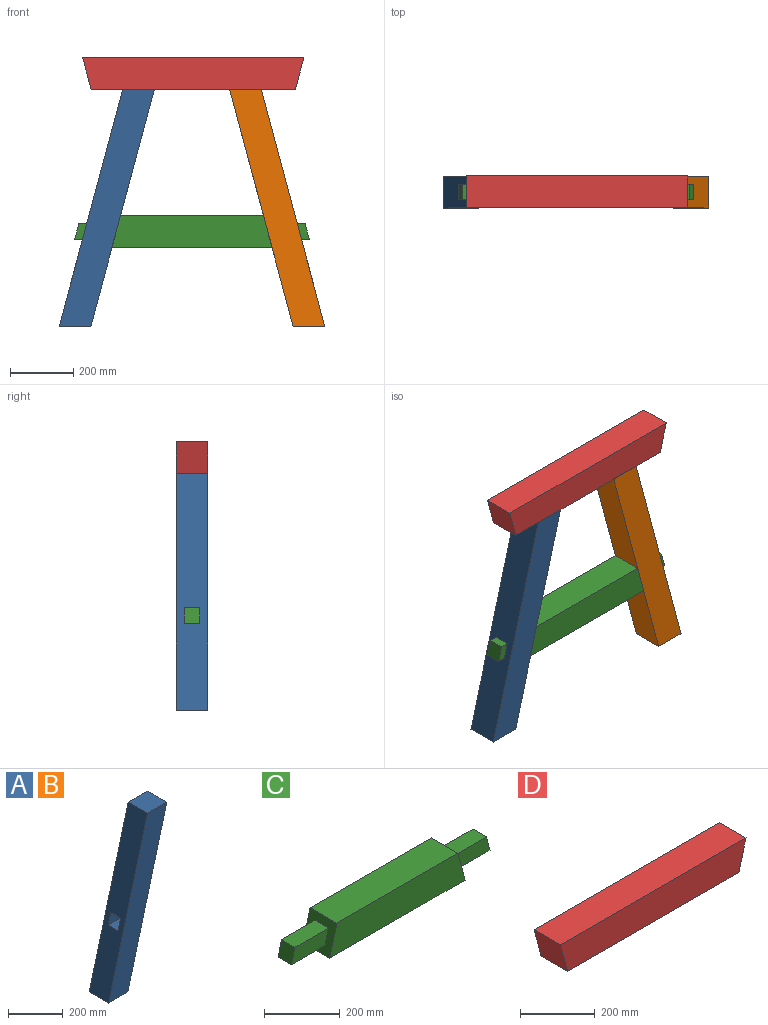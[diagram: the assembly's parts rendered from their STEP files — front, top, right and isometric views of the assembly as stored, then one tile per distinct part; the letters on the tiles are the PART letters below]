
ASSEMBLY  parts=4 mates=3
PART A: 10 faces, bbox 301x100x750 mm
  f0: plane 750x200.96mm, normal (-0.97,0,0.26), area 75057.5mm2, adj f2,f3,f4,f5,f6,f7,f8,f9
  f1: plane 750x200.96mm, normal (0.97,0,-0.26), area 75057.5mm2, adj f2,f3,f4,f5,f6,f7,f8,f9
  f2: plane 113.4x50mm, normal (0,1,0), area 5000mm2, adj f0,f1,f4,f8
  f3: plane 750x300.96mm, normal (0,-1,0), area 75000mm2, adj f0,f1,f5,f7
  f4: plane 100x50mm, normal (0,0,-1), area 5000mm2, adj f0,f1,f2,f9
  f5: plane 100x100mm, normal (0,0,1), area 10000mm2, adj f0,f1,f3,f6
  f6: plane 750x300.96mm, normal (0,1,0), area 75000mm2, adj f0,f1,f5,f7
  f7: plane 100x100mm, normal (0,0,-1), area 10000mm2, adj f0,f1,f3,f6
  f8: plane 100x50mm, normal (0,0,1), area 5000mm2, adj f0,f1,f2,f9
  f9: plane 113.4x50mm, normal (0,-1,0), area 5000mm2, adj f0,f1,f4,f8
PART B: same geometry as A
PART C: 16 faces, bbox 742.9x100x100 mm
  f0: plane 100x100mm, normal (0.97,0,0.26), area 7764.6mm2, adj f2,f3,f4,f5,f11,f12,f14,f15
  f1: plane 100x100mm, normal (-0.97,0,0.26), area 7764.6mm2, adj f2,f3,f4,f5,f6,f7,f9,f10
  f2: plane 452.71x100mm, normal (0,0,1), area 45270.7mm2, adj f0,f1,f4,f5
  f3: plane 506.3x100mm, normal (0,0,-1), area 50629.7mm2, adj f0,f1,f4,f5
  f4: plane 506.3x100mm, normal (0,-1,0), area 47950.2mm2, adj f0,f1,f2,f3
  f5: plane 506.3x100mm, normal (0,1,0), area 47950.2mm2, adj f0,f1,f2,f3
  f6: plane 125x50mm, normal (0,0,-1), area 6250mm2, adj f1,f8,f9,f10
  f7: plane 125x50mm, normal (0,0,1), area 6250mm2, adj f1,f8,f9,f10
  f8: plane 50x50mm, normal (-0.97,0,0.26), area 2588.2mm2, adj f6,f7,f9,f10
  f9: plane 138.4x50mm, normal (0,-1,0), area 6250mm2, adj f1,f6,f7,f8
  f10: plane 138.4x50mm, normal (0,1,0), area 6250mm2, adj f1,f6,f7,f8
  f11: plane 125x50mm, normal (0,0,1), area 6250mm2, adj f0,f13,f14,f15
  f12: plane 125x50mm, normal (0,0,-1), area 6250mm2, adj f0,f13,f14,f15
  f13: plane 50x50mm, normal (0.97,0,0.26), area 2588.2mm2, adj f11,f12,f14,f15
  f14: plane 138.4x50mm, normal (0,-1,0), area 6250mm2, adj f0,f11,f12,f13
  f15: plane 138.4x50mm, normal (0,1,0), area 6250mm2, adj f0,f11,f12,f13
PART D: 6 faces, bbox 700x100x100 mm
  f0: plane 700x100mm, normal (0,0,1), area 70000mm2, adj f1,f3,f4,f5
  f1: plane 100x100mm, normal (-0.97,0,-0.26), area 10352.8mm2, adj f0,f2,f4,f5
  f2: plane 646.41x100mm, normal (0,0,-1), area 64641mm2, adj f1,f3,f4,f5
  f3: plane 100x100mm, normal (0.97,0,-0.26), area 10352.8mm2, adj f0,f2,f4,f5
  f4: plane 700x100mm, normal (0,-1,0), area 67320.5mm2, adj f0,f1,f2,f3
  f5: plane 700x100mm, normal (0,1,0), area 67320.5mm2, adj f0,f1,f2,f3
PLACE A t=(-404.23,-206.37,25)mm fixed
PLACE B rot(axis=(0,0,1),180deg) t=(1.42,-306.37,25)mm
PLACE C t=(-283.07,-256.37,-26.6)mm fixed
PLACE D t=(-488.4,-206.37,455.02)mm
MATE fastened B.f8 <-> C.f12  axis (0,0,1) through (45.05,-231.37,-76.6)mm
MATE fastened D.f2 <-> A.f5  axis (0,0,1) through (-520.58,-306.37,398.4)mm
MATE fastened C.f6 <-> A.f8  axis (0,0,1) through (-447.85,-281.37,-76.6)mm
